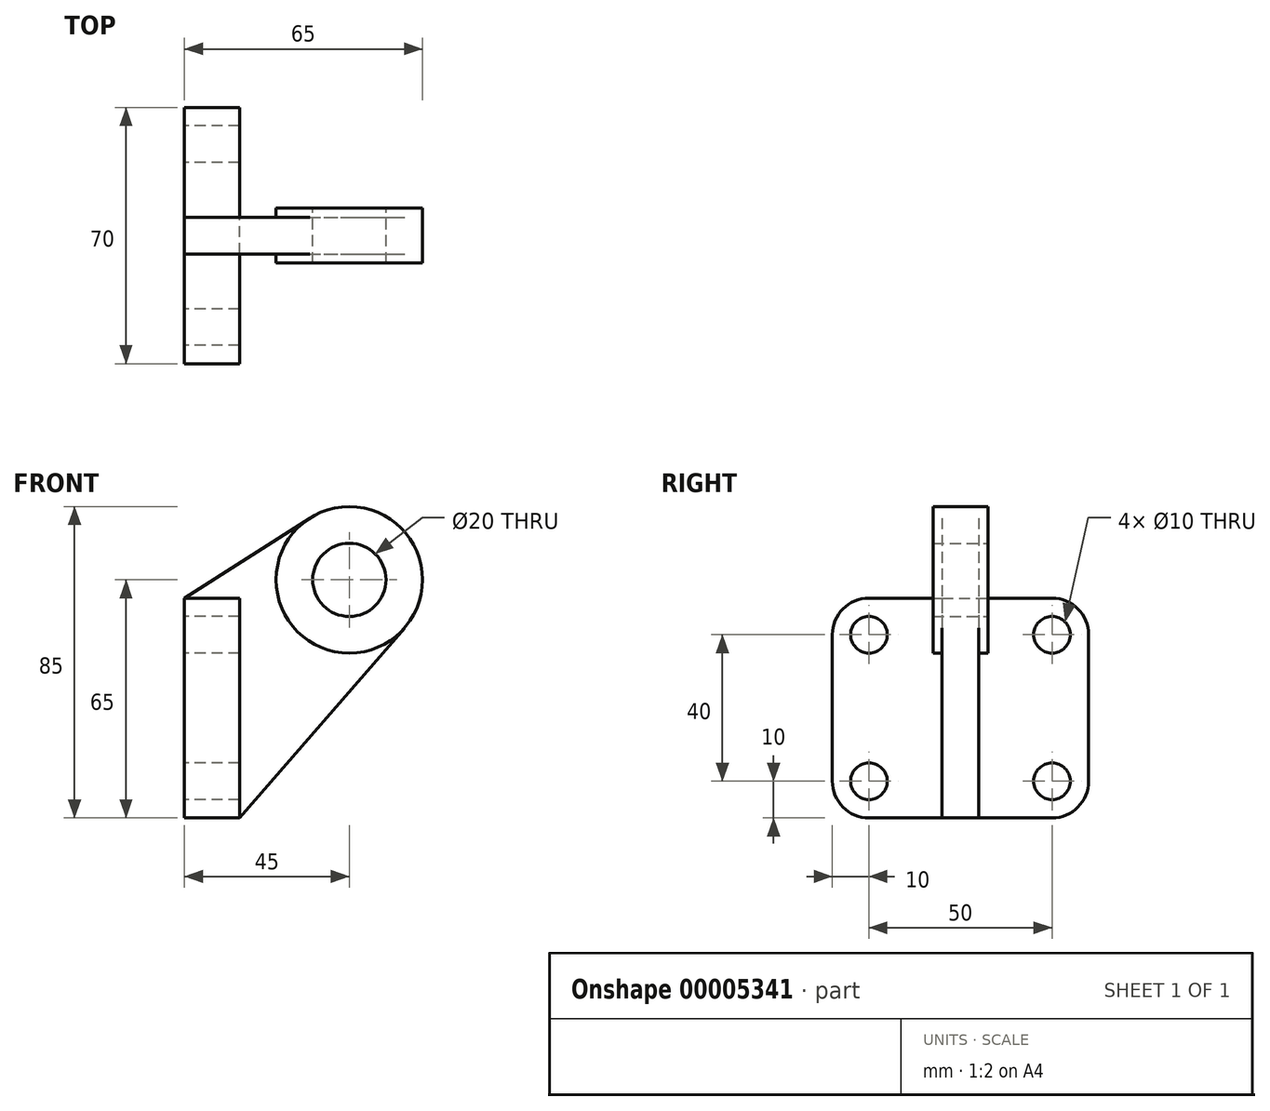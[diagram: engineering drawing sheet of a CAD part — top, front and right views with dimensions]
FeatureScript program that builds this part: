
annotation { "Feature Type Name" : "Feature", "Feature Type Description" : "" }
export const myFeature = defineFeature(function(context is Context, id is Id, definition is map)
    precondition{}
    {
        {
            var Q0;
            Q0=qCreatedBy(makeId("Right.planeOp"),FACE);
            var sketch = newSketch(context, id + "F0", { "sketchPlane" : qUnion([Q0])});
            skLineSegment(sketch, "E0.rect.bottom", {"start": v(-25, -30) * mm, "end": v(25, -30) * mm});
            skLineSegment(sketch, "E0.rect.top", {"start": v(-25, 30) * mm, "end": v(25, 30) * mm});
            skLineSegment(sketch, "E0.rect.left", {"start": v(-35, -20) * mm, "end": v(-35, 20) * mm});
            skLineSegment(sketch, "E0.rect.right", {"start": v(35, -20) * mm, "end": v(35, 20) * mm});
            skPoint(sketch, "E0.rect.middle", {"position": v(0, 0) * mm});
            skPoint(sketch, "E1.visualSharp", {"position": v(-35, 30) * mm});
            skArc(sketch, "E1.filletArc", {"start": v(-25, 30) * mm, "mid": v(-32.07, 27.07) * mm, "end": v(-35, 20) * mm});
            skPoint(sketch, "E2.visualSharp", {"position": v(-35, -30) * mm});
            skArc(sketch, "E2.filletArc", {"start": v(-35, -20) * mm, "mid": v(-32.07, -27.07) * mm, "end": v(-25, -30) * mm});
            skPoint(sketch, "E3.visualSharp", {"position": v(35, -30) * mm});
            skArc(sketch, "E3.filletArc", {"start": v(25, -30) * mm, "mid": v(32.07, -27.07) * mm, "end": v(35, -20) * mm});
            skPoint(sketch, "E4.visualSharp", {"position": v(35, 30) * mm});
            skArc(sketch, "E4.filletArc", {"start": v(35, 20) * mm, "mid": v(32.07, 27.07) * mm, "end": v(25, 30) * mm});
            skCircle(sketch, "E5", {"center": v(25, 20) * mm, "radius": 5 * mm});
            skCircle(sketch, "E6", {"center": v(25, -20) * mm, "radius": 5 * mm});
            skCircle(sketch, "E7", {"center": v(-25, -20) * mm, "radius": 5 * mm});
            skCircle(sketch, "E8", {"center": v(-25, 20) * mm, "radius": 5 * mm});
            skSolve(sketch);
        }
        {
            var Q0;
            Q0 = qSketchRegion(id + "F0", true);
            extrude(context, id + "F1", {"entities" : qUnion([Q0]), "depth" : 15 * mm});
        }
        {
            var Q0;
            Q0=qCreatedBy(makeId("Front.planeOp"),FACE);
            var sketch = newSketch(context, id + "F2", { "sketchPlane" : qUnion([Q0])});
            skCircle(sketch, "E9", {"center": v(45, 35) * mm, "radius": 10 * mm});
            skCircle(sketch, "E10", {"center": v(45, 35) * mm, "radius": 20 * mm});
            skLineSegment(sketch, "E11", {"start": v(34.24, 51.86) * mm, "end": v(0, 30) * mm});
            skLineSegment(sketch, "E12", {"start": v(0, 30) * mm, "end": v(15, 30) * mm});
            skLineSegment(sketch, "E13", {"start": v(15, 30) * mm, "end": v(15, -30) * mm});
            skLineSegment(sketch, "E14", {"start": v(15, -30) * mm, "end": v(60.1, 21.88) * mm});
            skSolve(sketch);
        }
        {
            var Q0;
            {var subQ1=sQuery(id+"F2.wireOp",EDGE,"E11");Q0=makeQuery(id+"F2.imprint","IMPRINT",FACE,{"disambiguationData":[TD([[makeQuery(id+"F2.imprint","IMPRINT",EDGE,{"derivedFrom":subQ1}),1.0]])]});}
            extrude(context, id + "F3", {"entities" : qUnion([Q0]), "operationType" : NewBodyOperationType.ADD, "endBound" : BoundingType.SYMMETRIC, "depth" : 10 * mm});
        }
        {
            var Q0;
            Q0=makeQuery(id+"F2.imprint","IMPRINT",FACE,{"disambiguationData":[TD([[makeQuery(id+"F2.imprint","IMPRINT",EDGE,{"derivedFrom":sQuery(id+"F2.wireOp",EDGE,"E9")}),-1.0]])]});
            extrude(context, id + "F4", {"entities" : qUnion([Q0]), "operationType" : NewBodyOperationType.ADD, "endBound" : BoundingType.SYMMETRIC, "depth" : 15 * mm});
        }
    });
